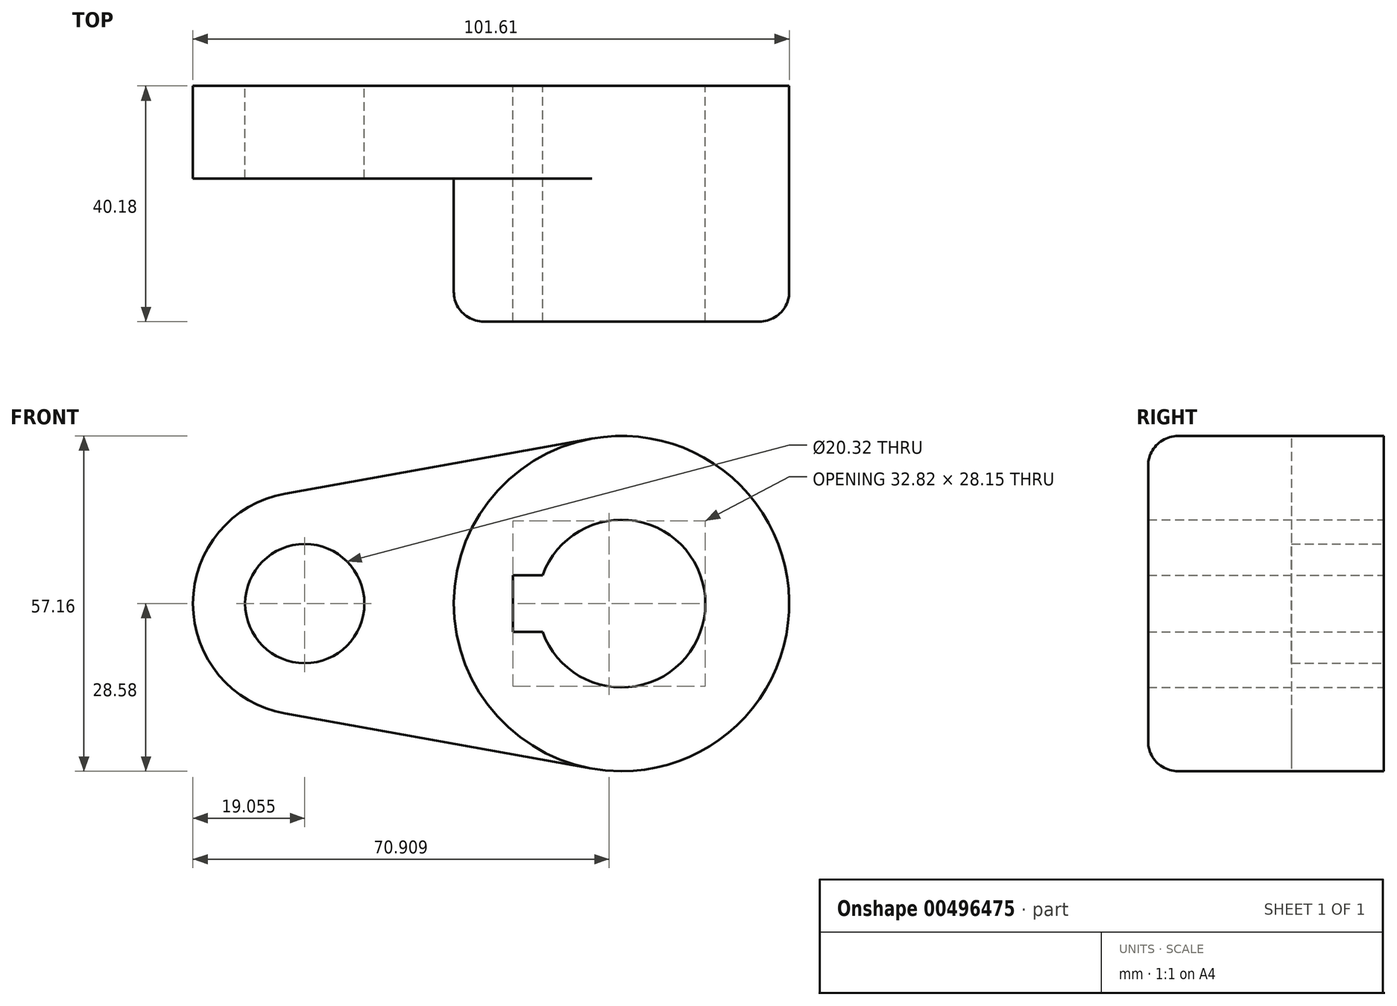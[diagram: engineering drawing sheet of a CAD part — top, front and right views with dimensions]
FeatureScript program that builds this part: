
annotation { "Feature Type Name" : "Feature", "Feature Type Description" : "" }
export const myFeature = defineFeature(function(context is Context, id is Id, definition is map)
    precondition{}
    {
        {
            var Q0;
            Q0=qCreatedBy(makeId("Front.planeOp"),FACE);
            var sketch = newSketch(context, id + "F0", { "sketchPlane" : qUnion([Q0])});
            skCircle(sketch, "E0", {"center": v(0, 0) * mm, "radius": 28.58 * mm});
            skCircle(sketch, "E1", {"center": v(0, 0) * mm, "radius": 14.29 * mm});
            skLineSegment(sketch, "E2.bottom", {"start": v(-18.53, 4.83) * mm, "end": v(-10.05, 4.83) * mm});
            skLineSegment(sketch, "E2.top", {"start": v(-18.53, -4.83) * mm, "end": v(-10.05, -4.83) * mm});
            skLineSegment(sketch, "E2.left", {"start": v(-18.53, 4.83) * mm, "end": v(-18.53, -4.83) * mm});
            skLineSegment(sketch, "E2.right", {"start": v(-10.05, 4.83) * mm, "end": v(-10.05, -4.83) * mm});
            skPoint(sketch, "E2.middle", {"position": v(-14.29, 0) * mm});
            skCircle(sketch, "E3", {"center": v(-53.98, 0) * mm, "radius": 19.05 * mm});
            skCircle(sketch, "E4", {"center": v(-53.98, 0) * mm, "radius": 10.16 * mm});
            skLineSegment(sketch, "E5", {"start": v(-5.04, 28.13) * mm, "end": v(-57.34, 18.75) * mm});
            skLineSegment(sketch, "E6", {"start": v(-57.34, -18.75) * mm, "end": v(-5.04, -28.13) * mm});
            skSolve(sketch);
        }
        {
            var Q0;
            Q0=makeQuery(id+"F0.imprint","IMPRINT",FACE,{"disambiguationData":[TD([[makeQuery(id+"F0.imprint","IMPRINT",EDGE,{"derivedFrom":sQuery(id+"F0.wireOp",EDGE,"E0")}),1.0]])]});
            extrude(context, id + "F1", {"entities" : qUnion([Q0]), "depth" : 40.18 * mm, "offsetDistance" : 25.4 * mm});
        }
        {
            var Q0;
            {var subQ0=sQuery(id+"F0.wireOp",EDGE,"E5");Q0=makeQuery(id+"F0.imprint","IMPRINT",FACE,{"disambiguationData":[TD([[makeQuery(id+"F0.imprint","IMPRINT",EDGE,{"derivedFrom":subQ0}),1.0]])]});}
            extrude(context, id + "F2", {"entities" : qUnion([Q0]), "operationType" : NewBodyOperationType.ADD, "depth" : 15.77 * mm, "offsetDistance" : 25.4 * mm});
        }
        {
            var Q0;
            Q0=makeQuery(id+"F0.imprint","IMPRINT",FACE,{"disambiguationData":[TD([[makeQuery(id+"F0.imprint","IMPRINT",EDGE,{"derivedFrom":sQuery(id+"F0.wireOp",EDGE,"E4")}),-1.0]])]});
            extrude(context, id + "F3", {"entities" : qUnion([Q0]), "operationType" : NewBodyOperationType.ADD, "depth" : 15.77 * mm, "offsetDistance" : 25.4 * mm});
        }
        {
            var Q0;
            Q0=makeQuery(id+"F1.opExtrude","CAP_EDGE",EDGE,{"disambiguationData":[OSD([sQuery(id+"F0.wireOp",EDGE,"E0")])],"isStart":false});
            fillet(context, id + "F4", {"entities" : qUnion([Q0]), "radius" : 5.08 * mm, "tangentPropagation" : true, "allowEdgeOverflow" : false});
        }
    });
